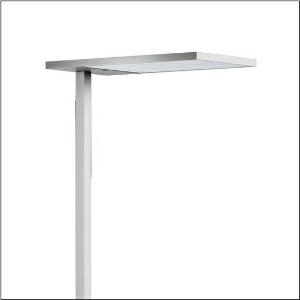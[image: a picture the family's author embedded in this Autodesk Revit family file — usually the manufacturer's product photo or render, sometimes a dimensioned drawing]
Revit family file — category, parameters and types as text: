
# Revit family: silica_21_floor_r_51mx53sg4ds
name_source: partatom
category: Lighting Fixtures
units: mm (PartAtom-declared; Revit-internal decimal feet)

## family parameters
Cut with Voids When Loaded = No
Host = Face
Light Source = No
Part Type = Normal
Room Calculation Point = No
Round Connector Dimension = Use Diameter
Shared = No

## types (1)
- Silica 21 Floor R (1 x LED, 15000 lm, 106.4 W, 4000K)
    Apparent Load = 106 VA
    CIE Flux Codes = 54 86 97 13 100
    Color Rendering = 80
    Color Temperature = 4000K
    Default Elevation = 1800 mm
    Description = Silica® 21 Floor R, floorstanding luminaire, of PMMA, primary optical cover: prismatic diffuser, of PMMA, CAT 2 (L<= 3000cd/m²), light emission: indirect/direct distribution, primary light characteristic: symmetric, primary optical cover: cover panel, of PMMA, installation type: not mounted, LED, rated luminous flux: 15.000lm, luminous efficacy: 141lm/W, light colour: 840, colour temperature: 4000K, control gear: DALI 2, daylight-dependent control, mains connection: 230V, AC, 50/60Hz, connection cable included, cable length: 2,5m, rated input power: 106.4W, luminaire head, of aluminium, powder-coated, metallic grey (RAL 9006), length: 671mm, width: 371mm, height: 2010mm, supporting column, angular, of aluminium, powder-coated, metallic grey (RAL 9006), baseplate, of steel, powder-coated, metallic grey (RAL 9006), sensor module PR3-S, local control - self-sufficient standalone sensors, equipment: master, dimmable, protection rating (complete): IP20, insulation class (complete): insulation class I (protective earthing), certification: CE, permissible operating ambient temperature: 0..+35°C, standard: EN 50419, packaging unit: 1 piece
    Height = 18 mm
    Lamp = 1 x LED
    Lamp Light Flux = 15000 lm
    Lamp Power = 106.4 W
    Lamp count = 1
    Length = 650 mm
    Luminous efficacy = 141 lm/W
    Manufacturer = Siteco
    ModVariant = No
    Model = 51MX53SG4DS
    Mounting Place = Floor
    Mounting Type = Freestanding
    Number of Poles = 1
    OnlyDefault = Yes
    Power Factor = 1
    Product Name = Silica 21 Floor R
    Product group = floorstanding luminaire
    ProductGroupID = 1302
    Protection Class = Protection class I
    Protection Degree = IP 20
    RLX_Detail_Level = 1
    RLX_Emergency_Light_Flux = 0 lm
    RLX_Emergency_Type = 0
    RLX_Emergency_Type_DB = No
    RlxData = <blob elided: 20409 chars, md5=4beb347b>
    Socket = socket
    Standby Power = 0 W
    System Light Flux = 15000 lm
    System Power = 106 W
    Type Comments = Product without accessories
    Type Image = l_1006716.jpg
    URL = http://relux.com
    VarID = ---
    Voltage = 0 V
    Weight = 0.00 kg
    Width = 350 mm

## geometry (parser evidence)
native form markers: Blend x4, Sweep x15
no freeform markers — native parametric forms only
